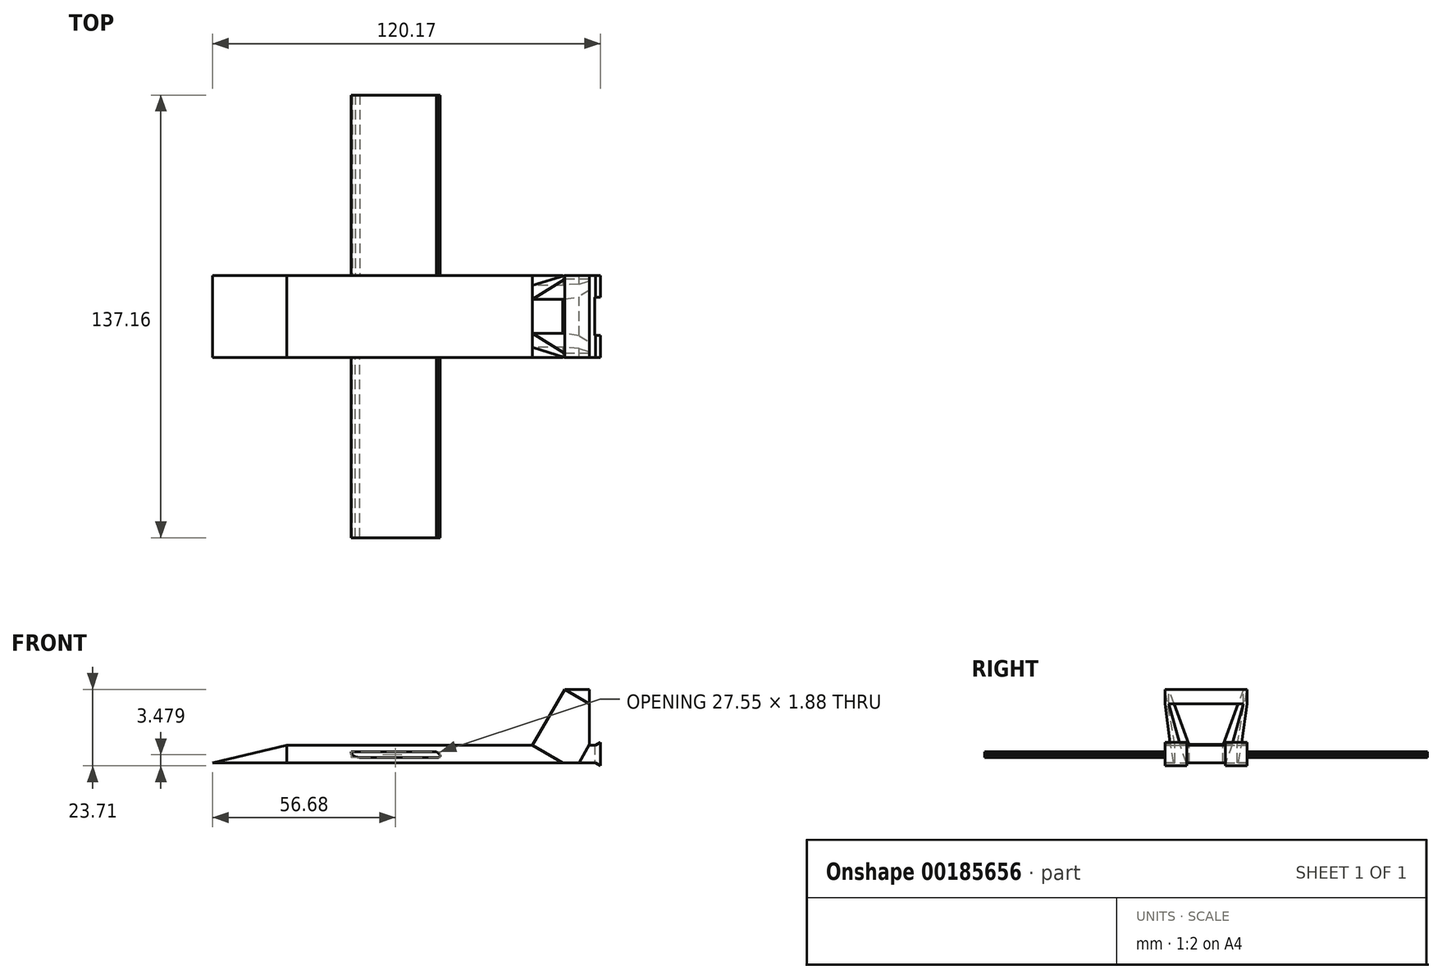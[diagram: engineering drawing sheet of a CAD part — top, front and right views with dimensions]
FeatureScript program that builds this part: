
annotation { "Feature Type Name" : "Feature", "Feature Type Description" : "" }
export const myFeature = defineFeature(function(context is Context, id is Id, definition is map)
    precondition{}
    {
        {
            var Q0;
            Q0=qCreatedBy(makeId("Front.planeOp"),FACE);
            var sketch = newSketch(context, id + "F0", { "sketchPlane" : qUnion([Q0])});
            skLineSegment(sketch, "E0", {"start": v(-62.7, 0) * mm, "end": v(-39.67, 5.47) * mm});
            skLineSegment(sketch, "E1", {"start": v(-39.67, 5.47) * mm, "end": v(55.9, 5.47) * mm});
            skLineSegment(sketch, "E2", {"start": v(55.9, 5.47) * mm, "end": v(55.9, 0) * mm});
            skLineSegment(sketch, "E3", {"start": v(55.9, 0) * mm, "end": v(-62.7, 0) * mm});
            skLineSegment(sketch, "E4", {"start": v(-19.78, 3.45) * mm, "end": v(6.64, 3.45) * mm});
            skLineSegment(sketch, "E5", {"start": v(6.64, 3.45) * mm, "end": v(7.2, 3.06) * mm});
            skLineSegment(sketch, "E6", {"start": v(7.2, 3.06) * mm, "end": v(7.75, 2.44) * mm});
            skLineSegment(sketch, "E7", {"start": v(7.75, 2.44) * mm, "end": v(7.75, 1.9) * mm});
            skLineSegment(sketch, "E8", {"start": v(7.75, 1.9) * mm, "end": v(7.2, 1.57) * mm});
            skLineSegment(sketch, "E9", {"start": v(7.2, 1.57) * mm, "end": v(6.64, 1.57) * mm});
            skLineSegment(sketch, "E10", {"start": v(6.64, 1.57) * mm, "end": v(-17.16, 1.57) * mm});
            skLineSegment(sketch, "E11", {"start": v(-17.16, 1.57) * mm, "end": v(-18.5, 1.9) * mm});
            skLineSegment(sketch, "E12", {"start": v(-18.5, 1.9) * mm, "end": v(-19.42, 2.44) * mm});
            skLineSegment(sketch, "E13", {"start": v(-19.42, 2.44) * mm, "end": v(-19.8, 3.06) * mm});
            skLineSegment(sketch, "E14", {"start": v(-19.8, 3.06) * mm, "end": v(-19.78, 3.45) * mm});
            skLineSegment(sketch, "E15", {"start": v(36.34, 5.47) * mm, "end": v(46.35, 22.74) * mm});
            skLineSegment(sketch, "E16", {"start": v(46.35, 22.74) * mm, "end": v(54.07, 22.74) * mm});
            skLineSegment(sketch, "E17", {"start": v(54.07, 22.74) * mm, "end": v(54.07, 5.47) * mm});
            skLineSegment(sketch, "E18", {"start": v(55.9, 5.47) * mm, "end": v(57.47, 6.36) * mm});
            skLineSegment(sketch, "E19", {"start": v(57.47, 6.36) * mm, "end": v(57.47, -0.97) * mm});
            skLineSegment(sketch, "E20", {"start": v(57.47, -0.97) * mm, "end": v(55.9, 0) * mm});
            skLineSegment(sketch, "E21", {"start": v(-39.67, 5.47) * mm, "end": v(-39.67, 0) * mm});
            skSolve(sketch);
        }
        {
            var Q0;
            {var subQ0=sQuery(id+"F0.wireOp",EDGE,"E0");Q0=makeQuery(id+"F0.imprint","IMPRINT",FACE,{"disambiguationData":[TD([[makeQuery(id+"F0.imprint","IMPRINT",EDGE,{"derivedFrom":subQ0}),-1.0]])]});}
            extrude(context, id + "F1", {"entities" : qUnion([Q0]), "depth" : 25.4 * mm});
        }
        {
            var Q0;
            Q0=makeQuery(id+"F0.imprint","IMPRINT",FACE,{"disambiguationData":[TD([[makeQuery(id+"F0.imprint","IMPRINT",EDGE,{"derivedFrom":sQuery(id+"F0.wireOp",EDGE,"E4")}),-1.0]])]});
            extrude(context, id + "F2", {"entities" : qUnion([Q0]), "depth" : 81.28 * mm});
        }
        {
            var Q0;
            {var subQ1=sQuery(id+"F0.wireOp",EDGE,"E2");Q0=makeQuery(id+"F0.imprint","IMPRINT",FACE,{"disambiguationData":[TD([[makeQuery(id+"F0.imprint","IMPRINT",EDGE,{"derivedFrom":subQ1}),-1.0]])]});}
            extrude(context, id + "F3", {"entities" : qUnion([Q0]), "depth" : 25.4 * mm});
        }
        {
            var Q0;
            {var subQ0=sQuery(id+"F0.wireOp",EDGE,"E15");Q0=makeQuery(id+"F0.imprint","IMPRINT",FACE,{"disambiguationData":[TD([[makeQuery(id+"F0.imprint","IMPRINT",EDGE,{"derivedFrom":subQ0}),-1.0]])]});}
            extrude(context, id + "F4", {"entities" : qUnion([Q0]), "operationType" : NewBodyOperationType.ADD, "depth" : 25.4 * mm});
        }
        {
            var Q0;
            Q0=makeQuery(id+"F0.imprint","IMPRINT",FACE,{"disambiguationData":[TD([[makeQuery(id+"F0.imprint","IMPRINT",EDGE,{"derivedFrom":sQuery(id+"F0.wireOp",EDGE,"E2")}),1.0]])]});
            extrude(context, id + "F5", {"entities" : qUnion([Q0]), "operationType" : NewBodyOperationType.ADD, "depth" : 25.4 * mm});
        }
        {
            var Q0;
            Q0=makeQuery(id+"F0.imprint","IMPRINT",FACE,{"disambiguationData":[TD([[makeQuery(id+"F0.imprint","IMPRINT",EDGE,{"derivedFrom":sQuery(id+"F0.wireOp",EDGE,"E4")}),-1.0]])]});
            extrude(context, id + "F6", {"entities" : qUnion([Q0]), "operationType" : NewBodyOperationType.ADD, "oppositeDirection" : true, "depth" : 55.88 * mm});
        }
        {
            var Q0;
            Q0=makeQuery(id+"F4.opExtrude","SWEPT_FACE",FACE,{"disambiguationData":[OSD([sQuery(id+"F0.wireOp",EDGE,"E15")])]});
            var sketch = newSketch(context, id + "F7", { "sketchPlane" : qUnion([Q0])});
            skLineSegment(sketch, "E22", {"start": v(1.15, 42.9) * mm, "end": v(7.44, 22.94) * mm});
            skLineSegment(sketch, "E23", {"start": v(7.44, 22.94) * mm, "end": v(3.06, 22.94) * mm});
            skLineSegment(sketch, "E24", {"start": v(3.06, 22.94) * mm, "end": v(0, 42.9) * mm});
            skLineSegment(sketch, "E25", {"start": v(0, 42.9) * mm, "end": v(1.15, 42.9) * mm});
            skLineSegment(sketch, "E26", {"start": v(22.3, 22.94) * mm, "end": v(25.4, 42.9) * mm});
            skLineSegment(sketch, "E27", {"start": v(25.4, 42.9) * mm, "end": v(24.22, 42.9) * mm});
            skLineSegment(sketch, "E28", {"start": v(22.3, 22.94) * mm, "end": v(17.92, 22.94) * mm});
            skLineSegment(sketch, "E29", {"start": v(17.92, 22.94) * mm, "end": v(24.22, 42.9) * mm});
            skSolve(sketch);
        }
        {
            var Q0;
            {var subQ0=sQuery(id+"F7.wireOp",EDGE,"E24");Q0=makeQuery(id+"F7.imprint","IMPRINT",FACE,{"disambiguationData":[TD([[makeQuery(id+"F7.imprint","IMPRINT",EDGE,{"derivedFrom":subQ0}),1.0]])]});}
            extrude(context, id + "F8", {"entities" : qUnion([Q0]), "operationType" : NewBodyOperationType.REMOVE, "oppositeDirection" : true, "depth" : 15.24 * mm});
        }
        {
            var Q0;
            {var subQ0=sQuery(id+"F7.wireOp",EDGE,"E26");Q0=makeQuery(id+"F7.imprint","IMPRINT",FACE,{"disambiguationData":[TD([[makeQuery(id+"F7.imprint","IMPRINT",EDGE,{"derivedFrom":subQ0}),-1.0]])]});}
            extrude(context, id + "F9", {"entities" : qUnion([Q0]), "operationType" : NewBodyOperationType.REMOVE, "oppositeDirection" : true, "depth" : 15.24 * mm});
        }
        {
            var Q0;
            Q0=makeQuery(id+"F5.opExtrude","SWEPT_FACE",FACE,{"disambiguationData":[OSD([sQuery(id+"F0.wireOp",EDGE,"E19")])]});
            var sketch = newSketch(context, id + "F10", { "sketchPlane" : qUnion([Q0])});
            skLineSegment(sketch, "E30.bottom", {"start": v(-6.75, 6.36) * mm, "end": v(-18.65, 6.36) * mm});
            skLineSegment(sketch, "E30.top", {"start": v(-6.75, -0.97) * mm, "end": v(-18.65, -0.97) * mm});
            skLineSegment(sketch, "E30.left", {"start": v(-6.75, 6.36) * mm, "end": v(-6.75, -0.97) * mm});
            skLineSegment(sketch, "E30.right", {"start": v(-18.65, 6.36) * mm, "end": v(-18.65, -0.97) * mm});
            skPoint(sketch, "E30.middle", {"position": v(-12.7, 2.7) * mm});
            skPoint(sketch, "E30.middle.positionSnap0", {"position": v(0, 2.7) * mm});
            skPoint(sketch, "E30.middle.positionSnap1", {"position": v(-12.7, 6.36) * mm});
            skPoint(sketch, "E30.centerSnap0", {"position": v(0, 2.7) * mm});
            skPoint(sketch, "E30.centerSnap1", {"position": v(-12.7, 6.36) * mm});
            skSolve(sketch);
        }
        {
            var Q0;
            Q0=makeQuery(id+"F10.imprint","IMPRINT",FACE,{"disambiguationData":[TD([[makeQuery(id+"F10.imprint","IMPRINT",EDGE,{"derivedFrom":sQuery(id+"F10.wireOp",EDGE,"E30.bottom")}),-1.0]])]});
            extrude(context, id + "F11", {"entities" : qUnion([Q0]), "operationType" : NewBodyOperationType.REMOVE, "oppositeDirection" : true, "depth" : 1.78 * mm});
        }
        {
            var Q0;
            {var subQ0=sQuery(id+"F7.wireOp",EDGE,"E22");Q0=makeQuery(id+"F7.imprint","IMPRINT",FACE,{"disambiguationData":[TD([[makeQuery(id+"F7.imprint","IMPRINT",EDGE,{"derivedFrom":subQ0}),1.0]])]});}
            extrude(context, id + "F12", {"entities" : qUnion([Q0]), "operationType" : NewBodyOperationType.REMOVE, "oppositeDirection" : true, "depth" : 15.24 * mm});
        }
    });
